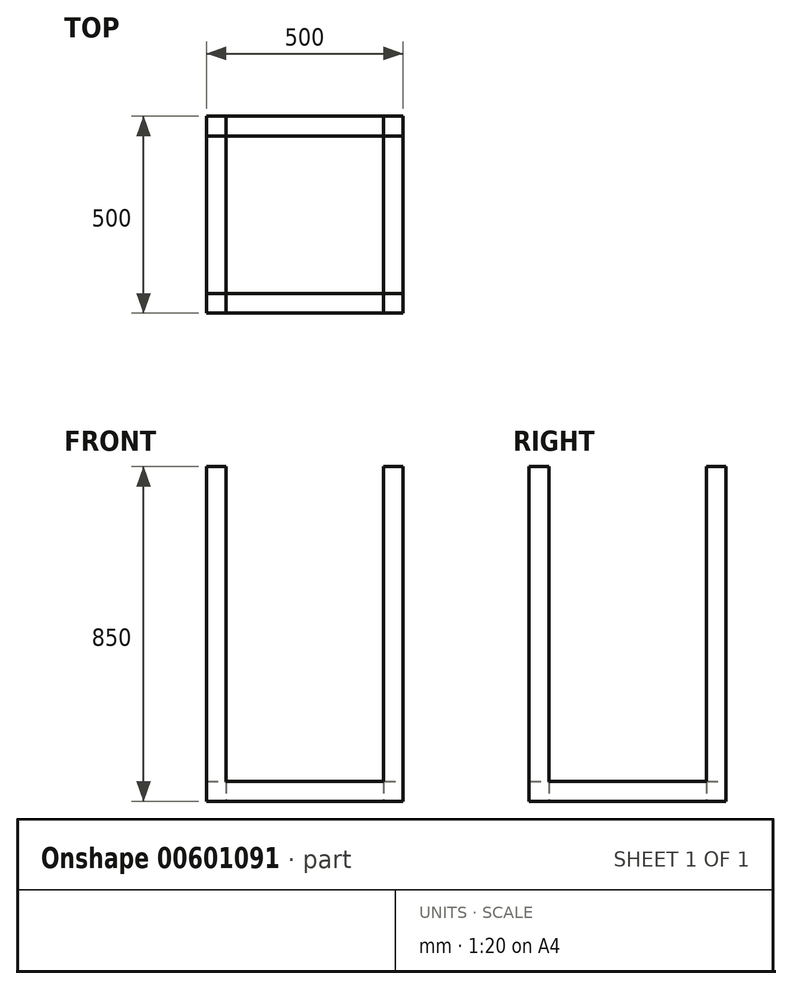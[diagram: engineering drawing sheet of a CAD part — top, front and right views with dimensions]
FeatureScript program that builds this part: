
annotation { "Feature Type Name" : "Feature", "Feature Type Description" : "" }
export const myFeature = defineFeature(function(context is Context, id is Id, definition is map)
    precondition{}
    {
        {
            var Q0;
            Q0=qCreatedBy(makeId("Top.planeOp"),FACE);
            var sketch = newSketch(context, id + "F0", { "sketchPlane" : qUnion([Q0])});
            skLineSegment(sketch, "E0.bottom", {"start": v(0, 0) * mm, "end": v(500, 0) * mm});
            skLineSegment(sketch, "E0.top", {"start": v(0, 500) * mm, "end": v(500, 500) * mm});
            skLineSegment(sketch, "E0.left", {"start": v(0, 0) * mm, "end": v(0, 500) * mm});
            skLineSegment(sketch, "E0.right", {"start": v(500, 0) * mm, "end": v(500, 500) * mm});
            skLineSegment(sketch, "E1.bottom", {"start": v(450, 450) * mm, "end": v(50, 450) * mm});
            skLineSegment(sketch, "E1.top", {"start": v(450, 50) * mm, "end": v(50, 50) * mm});
            skLineSegment(sketch, "E1.left", {"start": v(450, 450) * mm, "end": v(450, 50) * mm});
            skLineSegment(sketch, "E1.right", {"start": v(50, 450) * mm, "end": v(50, 50) * mm});
            skPoint(sketch, "E1.middle", {"position": v(250, 250) * mm});
            skLineSegment(sketch, "E2.bottom", {"start": v(0, 500) * mm, "end": v(50, 500) * mm});
            skLineSegment(sketch, "E2.top", {"start": v(0, 450) * mm, "end": v(50, 450) * mm});
            skLineSegment(sketch, "E2.left", {"start": v(0, 500) * mm, "end": v(0, 450) * mm});
            skLineSegment(sketch, "E2.right", {"start": v(50, 500) * mm, "end": v(50, 450) * mm});
            skLineSegment(sketch, "E3.bottom", {"start": v(450, 450) * mm, "end": v(500, 450) * mm});
            skLineSegment(sketch, "E3.top", {"start": v(450, 500) * mm, "end": v(500, 500) * mm});
            skLineSegment(sketch, "E3.left", {"start": v(450, 450) * mm, "end": v(450, 500) * mm});
            skLineSegment(sketch, "E3.right", {"start": v(500, 450) * mm, "end": v(500, 500) * mm});
            skLineSegment(sketch, "E4.bottom", {"start": v(450, 50) * mm, "end": v(500, 50) * mm});
            skLineSegment(sketch, "E4.top", {"start": v(450, 0) * mm, "end": v(500, 0) * mm});
            skLineSegment(sketch, "E4.left", {"start": v(450, 50) * mm, "end": v(450, 0) * mm});
            skLineSegment(sketch, "E4.right", {"start": v(500, 50) * mm, "end": v(500, 0) * mm});
            skLineSegment(sketch, "E5.bottom", {"start": v(0, 0) * mm, "end": v(50, 0) * mm});
            skLineSegment(sketch, "E5.top", {"start": v(0, 50) * mm, "end": v(50, 50) * mm});
            skLineSegment(sketch, "E5.left", {"start": v(0, 0) * mm, "end": v(0, 50) * mm});
            skLineSegment(sketch, "E5.right", {"start": v(50, 0) * mm, "end": v(50, 50) * mm});
            skSolve(sketch);
        }
        {
            var Q0;
            Q0=makeQuery(id+"F0.imprint","IMPRINT",FACE,{"disambiguationData":[TD([[makeQuery(id+"F0.imprint","IMPRINT",EDGE,{"derivedFrom":sQuery(id+"F0.wireOp",EDGE,"E2.bottom")}),-1.0]])]});
            var Q1;
            Q1=makeQuery(id+"F0.imprint","IMPRINT",FACE,{"disambiguationData":[TD([[makeQuery(id+"F0.imprint","IMPRINT",EDGE,{"derivedFrom":sQuery(id+"F0.wireOp",EDGE,"E0.top")}),-1.0]])]});
            var Q2;
            Q2=makeQuery(id+"F0.imprint","IMPRINT",FACE,{"disambiguationData":[TD([[makeQuery(id+"F0.imprint","IMPRINT",EDGE,{"derivedFrom":sQuery(id+"F0.wireOp",EDGE,"E3.bottom")}),1.0]])]});
            var Q3;
            Q3=makeQuery(id+"F0.imprint","IMPRINT",FACE,{"disambiguationData":[TD([[makeQuery(id+"F0.imprint","IMPRINT",EDGE,{"derivedFrom":sQuery(id+"F0.wireOp",EDGE,"E0.right")}),1.0]])]});
            var Q4;
            Q4=makeQuery(id+"F0.imprint","IMPRINT",FACE,{"disambiguationData":[TD([[makeQuery(id+"F0.imprint","IMPRINT",EDGE,{"derivedFrom":sQuery(id+"F0.wireOp",EDGE,"E4.bottom")}),-1.0]])]});
            var Q5;
            Q5=makeQuery(id+"F0.imprint","IMPRINT",FACE,{"disambiguationData":[TD([[makeQuery(id+"F0.imprint","IMPRINT",EDGE,{"derivedFrom":sQuery(id+"F0.wireOp",EDGE,"E0.bottom")}),1.0]])]});
            var Q6;
            Q6=makeQuery(id+"F0.imprint","IMPRINT",FACE,{"disambiguationData":[TD([[makeQuery(id+"F0.imprint","IMPRINT",EDGE,{"derivedFrom":sQuery(id+"F0.wireOp",EDGE,"E5.bottom")}),1.0]])]});
            var Q7;
            Q7=makeQuery(id+"F0.imprint","IMPRINT",FACE,{"disambiguationData":[TD([[makeQuery(id+"F0.imprint","IMPRINT",EDGE,{"derivedFrom":sQuery(id+"F0.wireOp",EDGE,"E0.left")}),-1.0]])]});
            extrude(context, id + "F1", {"entities" : qUnion([Q0, Q1, Q2, Q3, Q4, Q5, Q6, Q7]), "depth" : 50 * mm, "offsetDistance" : 25 * mm});
        }
        {
            var Q0;
            Q0=makeQuery(id+"F1.opExtrude","CAP_FACE",FACE,{"disambiguationData":[OSD([sQuery(id+"F0.wireOp",EDGE,"E0.bottom"),sQuery(id+"F0.wireOp",EDGE,"E0.top"),sQuery(id+"F0.wireOp",EDGE,"E0.left"),sQuery(id+"F0.wireOp",EDGE,"E0.right"),sQuery(id+"F0.wireOp",EDGE,"E1.bottom"),sQuery(id+"F0.wireOp",EDGE,"E1.top"),sQuery(id+"F0.wireOp",EDGE,"E1.left"),sQuery(id+"F0.wireOp",EDGE,"E1.right"),sQuery(id+"F0.wireOp",EDGE,"E2.bottom"),sQuery(id+"F0.wireOp",EDGE,"E2.left"),sQuery(id+"F0.wireOp",EDGE,"E3.top"),sQuery(id+"F0.wireOp",EDGE,"E3.right"),sQuery(id+"F0.wireOp",EDGE,"E4.top"),sQuery(id+"F0.wireOp",EDGE,"E4.right"),sQuery(id+"F0.wireOp",EDGE,"E5.bottom"),sQuery(id+"F0.wireOp",EDGE,"E5.left")])],"isStart":false});
            var sketch = newSketch(context, id + "F2", { "sketchPlane" : qUnion([Q0])});
            skLineSegment(sketch, "E6.bottom", {"start": v(0, 500) * mm, "end": v(50, 500) * mm});
            skLineSegment(sketch, "E6.top", {"start": v(0, 450) * mm, "end": v(50, 450) * mm});
            skLineSegment(sketch, "E6.left", {"start": v(0, 500) * mm, "end": v(0, 450) * mm});
            skLineSegment(sketch, "E6.right", {"start": v(50, 500) * mm, "end": v(50, 450) * mm});
            skLineSegment(sketch, "E7.bottom", {"start": v(450, 450) * mm, "end": v(500, 450) * mm});
            skLineSegment(sketch, "E7.top", {"start": v(450, 500) * mm, "end": v(500, 500) * mm});
            skLineSegment(sketch, "E7.left", {"start": v(450, 450) * mm, "end": v(450, 500) * mm});
            skLineSegment(sketch, "E7.right", {"start": v(500, 450) * mm, "end": v(500, 500) * mm});
            skLineSegment(sketch, "E8.bottom", {"start": v(450, 50) * mm, "end": v(500, 50) * mm});
            skLineSegment(sketch, "E8.top", {"start": v(450, 0) * mm, "end": v(500, 0) * mm});
            skLineSegment(sketch, "E8.left", {"start": v(450, 50) * mm, "end": v(450, 0) * mm});
            skLineSegment(sketch, "E8.right", {"start": v(500, 50) * mm, "end": v(500, 0) * mm});
            skLineSegment(sketch, "E9.bottom", {"start": v(0, 0) * mm, "end": v(50, 0) * mm});
            skLineSegment(sketch, "E9.top", {"start": v(0, 50) * mm, "end": v(50, 50) * mm});
            skLineSegment(sketch, "E9.left", {"start": v(0, 0) * mm, "end": v(0, 50) * mm});
            skLineSegment(sketch, "E9.right", {"start": v(50, 0) * mm, "end": v(50, 50) * mm});
            skSolve(sketch);
        }
        {
            var Q0;
            Q0=makeQuery(id+"F2.imprint","IMPRINT",FACE,{"disambiguationData":[TD([[makeQuery(id+"F2.imprint","IMPRINT",EDGE,{"derivedFrom":sQuery(id+"F2.wireOp",EDGE,"E6.bottom")}),-1.0]])]});
            var Q1;
            Q1=makeQuery(id+"F2.imprint","IMPRINT",FACE,{"disambiguationData":[TD([[makeQuery(id+"F2.imprint","IMPRINT",EDGE,{"derivedFrom":sQuery(id+"F2.wireOp",EDGE,"E7.bottom")}),1.0]])]});
            var Q2;
            Q2=makeQuery(id+"F2.imprint","IMPRINT",FACE,{"disambiguationData":[TD([[makeQuery(id+"F2.imprint","IMPRINT",EDGE,{"derivedFrom":sQuery(id+"F2.wireOp",EDGE,"E8.bottom")}),-1.0]])]});
            var Q3;
            Q3=makeQuery(id+"F2.imprint","IMPRINT",FACE,{"disambiguationData":[TD([[makeQuery(id+"F2.imprint","IMPRINT",EDGE,{"derivedFrom":sQuery(id+"F2.wireOp",EDGE,"E9.bottom")}),1.0]])]});
            extrude(context, id + "F3", {"entities" : qUnion([Q0, Q1, Q2, Q3]), "operationType" : NewBodyOperationType.ADD, "depth" : 800 * mm, "offsetDistance" : 25 * mm});
        }
    });
